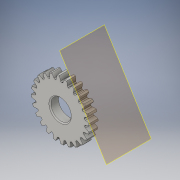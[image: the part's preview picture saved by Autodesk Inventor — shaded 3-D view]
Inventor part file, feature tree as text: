
AUTODESK INVENTOR PART (.ipt)
format: ipt  version: 2016 (Build 200138000, 138)  size: 668,160 bytes
history: native  units: in
note: dims shown in document units (in); Inventor stores cm internally (conversion verified against a paired STEP export)
features: plane x1, extrude x1, sketch x1, chamfer x1
ambient origin geometry x8: Origin, YZ Plane, XZ Plane, XY Plane, X Axis, Y Axis, Z Axis, Center Point
bodies: Solid1 (feature_tree)
feature tree (4):
  plane  "Work Plane1"
  extrude  "Extrusion1"  [1 undecoded]
  sketch  "Sketch1"  dims[d0=1.0in d1=0.0in]
  chamfer  "Chamfer1"  [1 undecoded]
note: 2 required parameter values undecoded (feature->parameter linkage not recoverable at this tier; creation-order binding heuristic only, values carry confidence <= 0.55)
